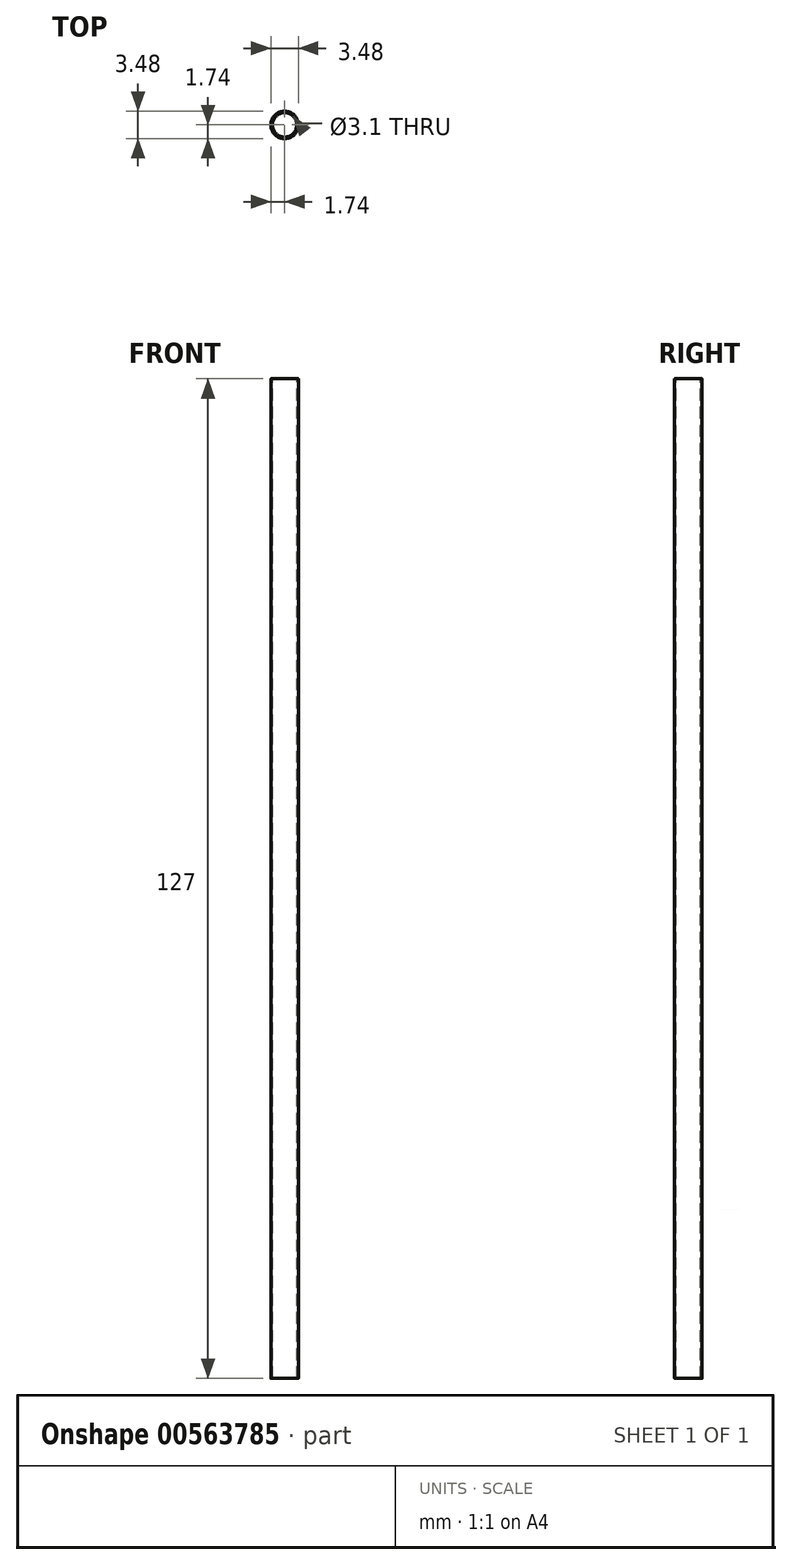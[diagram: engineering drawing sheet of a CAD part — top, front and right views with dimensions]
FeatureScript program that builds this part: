
annotation { "Feature Type Name" : "Feature", "Feature Type Description" : "" }
export const myFeature = defineFeature(function(context is Context, id is Id, definition is map)
    precondition{}
    {
        {
            var Q0;
            Q0=qCreatedBy(makeId("Front.planeOp"),FACE);
            var sketch = newSketch(context, id + "F0", { "sketchPlane" : qUnion([Q0])});
            skLineSegment(sketch, "E0", {"start": v(-1.55, 89.88) * mm, "end": v(-1.55, -37.07) * mm});
            skLineSegment(sketch, "E1.0", {"start": v(-1.74, 89.88) * mm, "end": v(-1.74, -37.07) * mm});
            skLineSegment(sketch, "E2", {"start": v(-1.57, -37.1) * mm, "end": v(-1.72, -37.1) * mm});
            skLineSegment(sketch, "E3", {"start": v(-1.57, 89.9) * mm, "end": v(-1.72, 89.9) * mm});
            skLineSegment(sketch, "E4", {"start": v(0, 89.9) * mm, "end": v(0, -37.1) * mm});
            skPoint(sketch, "E5.visualSharp", {"position": v(-1.55, -37.1) * mm});
            skArc(sketch, "E5.filletArc", {"start": v(-1.57, -37.1) * mm, "mid": v(-1.56, -37.1) * mm, "end": v(-1.55, -37.07) * mm});
            skPoint(sketch, "E6.visualSharp", {"position": v(-1.74, -37.1) * mm});
            skArc(sketch, "E6.filletArc", {"start": v(-1.74, -37.07) * mm, "mid": v(-1.74, -37.1) * mm, "end": v(-1.72, -37.1) * mm});
            skPoint(sketch, "E7.visualSharp", {"position": v(-1.55, 89.9) * mm});
            skArc(sketch, "E7.filletArc", {"start": v(-1.55, 89.88) * mm, "mid": v(-1.56, 89.9) * mm, "end": v(-1.57, 89.9) * mm});
            skPoint(sketch, "E8.visualSharp", {"position": v(-1.74, 89.9) * mm});
            skArc(sketch, "E8.filletArc", {"start": v(-1.72, 89.9) * mm, "mid": v(-1.74, 89.9) * mm, "end": v(-1.74, 89.88) * mm});
            skSolve(sketch);
        }
        {
            var Q0;
            Q0=makeQuery(id+"F0.imprint","IMPRINT",FACE,{"disambiguationData":[TD([[makeQuery(id+"F0.imprint","IMPRINT",EDGE,{"derivedFrom":sQuery(id+"F0.wireOp",EDGE,"E0")}),-1.0]])]});
            var Q1;
            Q1=sQuery(id+"F0.wireOp",EDGE,"E4");
            revolve(context, id + "F1", {"entities" : qUnion([Q0]), "axis" : qUnion([Q1]), "revolveType" : RevolveType.FULL});
        }
    });
